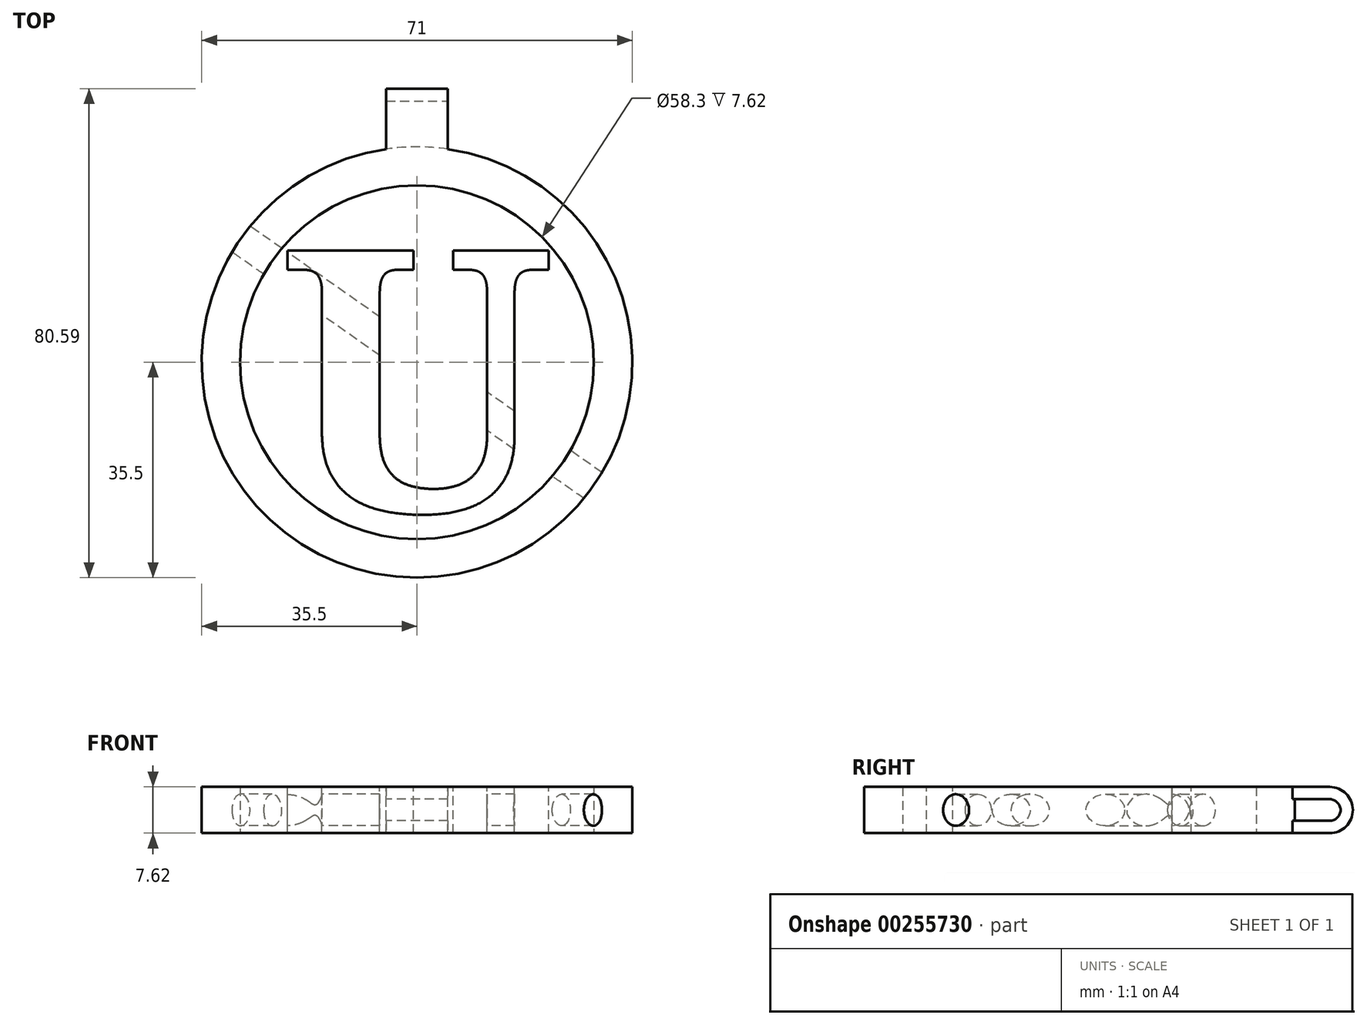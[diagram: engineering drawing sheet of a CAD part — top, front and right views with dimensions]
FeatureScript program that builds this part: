
annotation { "Feature Type Name" : "Feature", "Feature Type Description" : "" }
export const myFeature = defineFeature(function(context is Context, id is Id, definition is map)
    precondition{}
    {
        {
            var Q0;
            Q0=qCreatedBy(makeId("Top.planeOp"),FACE);
            var sketch = newSketch(context, id + "F0", { "sketchPlane" : qUnion([Q0])});
            skCircle(sketch, "E0", {"center": v(0, 0) * mm, "radius": 35.5 * mm});
            skCircle(sketch, "E1", {"center": v(0, 0) * mm, "radius": 29.15 * mm});
            skText(sketch, "E2", { "text": "U", "fontName": "NotoSerif-Bold.ttf"});
            const initialGuessF0  = {"E2": [-0.0225, -0.02528, 1, 0, 0.0438]};
            skSetInitialGuess(sketch, initialGuessF0);
            skSolve(sketch);
        }
        {
            var Q0;
            Q0 = qSketchRegion(id + "F0", true);
            extrude(context, id + "F1", {"entities" : qUnion([Q0]), "depth" : 7.62 * mm});
        }
        {
            var Q0;
            Q0=makeQuery(id+"F1.opExtrude","CAP_FACE",FACE,{"disambiguationData":[OSD([sQuery(id+"F0.wireOp",EDGE,"E0"),sQuery(id+"F0.wireOp",EDGE,"E1")])],"isStart":false});
            var sketch = newSketch(context, id + "F2", { "sketchPlane" : qUnion([Q0])});
            skText(sketch, "E3", { "text": "U", "fontName": "NotoSerif-Bold.ttf"});
            const initialGuessF2  = {"E3": [-0.02229, -0.02456, 1, 0, 0.04335]};
            skSetInitialGuess(sketch, initialGuessF2);
            skSolve(sketch);
        }
        {
            var Q0;
            Q0 = qSketchRegion(id + "F2", true);
            extrude(context, id + "F3", {"entities" : qUnion([Q0]), "oppositeDirection" : true, "depth" : 7.62 * mm});
        }
        {
            var Q0;
            Q0=qCreatedBy(makeId("Front.planeOp"),FACE);
            var Q1;
            Q1=makeQuery(id+"F3.opExtrude","SWEPT_EDGE",EDGE,{"disambiguationData":[OSD([sQuery(id+"F2.wireOp",EDGE,"E3.sketch_text.stroke-20"),sQuery(id+"F2.wireOp",EDGE,"E3.sketch_text.stroke-21")])]});
            cPlane(context, id + "F4", {"entities" : qUnion([Q0, Q1]), "cplaneType" : CPlaneType.LINE_ANGLE, "offset" : 25.4 * mm, "angle" : 55 * degree, "width" : 152.4 * mm, "height" : 152.4 * mm});
        }
        {
            var Q0;
            Q0=qCreatedBy(id+"F4.planeOp",FACE);
            var sketch = newSketch(context, id + "F5", { "sketchPlane" : qUnion([Q0])});
            skCircle(sketch, "E4", {"center": v(0, 3.81) * mm, "radius": 2.6 * mm});
            skSolve(sketch);
        }
        {
            var Q0;
            Q0 = qSketchRegion(id + "F5", true);
            extrude(context, id + "F6", {"entities" : qUnion([Q0]), "operationType" : NewBodyOperationType.REMOVE, "endBound" : BoundingType.THROUGH_ALL, "oppositeDirection" : true, "depth" : 25.4 * mm, "hasSecondDirection" : true, "secondDirectionBound" : SecondDirectionBoundingType.THROUGH_ALL, "secondDirectionOppositeDirection" : false, "secondDirectionDepth" : 25.4 * mm});
        }
        {
            var Q0;
            Q0=makeQuery(id+"F3.opExtrude","SWEPT_FACE",FACE,{"disambiguationData":[OSD([sQuery(id+"F2.wireOp",EDGE,"E3.sketch_text.stroke-44")])]});
            cPlane(context, id + "F7", {"entities" : qUnion([Q0]), "cplaneType" : CPlaneType.OFFSET, "offset" : 15.24 * mm, "width" : 152.4 * mm, "height" : 152.4 * mm});
        }
        {
            var Q0;
            Q0=qCreatedBy(id+"F7.planeOp",FACE);
            var sketch = newSketch(context, id + "F8", { "sketchPlane" : qUnion([Q0])});
            skLineSegment(sketch, "E5.bottom", {"start": v(-5.08, 7.62) * mm, "end": v(5.08, 7.62) * mm});
            skLineSegment(sketch, "E5.top", {"start": v(-5.08, 5.59) * mm, "end": v(5.08, 5.59) * mm});
            skLineSegment(sketch, "E5.left", {"start": v(-5.08, 7.62) * mm, "end": v(-5.08, 5.59) * mm});
            skLineSegment(sketch, "E5.right", {"start": v(5.08, 7.62) * mm, "end": v(5.08, 5.59) * mm});
            skLineSegment(sketch, "E6.bottom", {"start": v(-5.08, 2.03) * mm, "end": v(5.08, 2.03) * mm});
            skLineSegment(sketch, "E6.top", {"start": v(-5.08, 0) * mm, "end": v(5.08, 0) * mm});
            skLineSegment(sketch, "E6.left", {"start": v(-5.08, 2.03) * mm, "end": v(-5.08, 0) * mm});
            skLineSegment(sketch, "E6.right", {"start": v(5.08, 2.03) * mm, "end": v(5.08, 0) * mm});
            skSolve(sketch);
        }
        {
            var Q0;
            Q0 = qSketchRegion(id + "F8", true);
            extrude(context, id + "F9", {"entities" : qUnion([Q0]), "operationType" : NewBodyOperationType.ADD, "depth" : 7.62 * mm});
        }
        {
            var Q0;
            Q0=makeQuery(id+"F9.opExtrude","SWEPT_FACE",FACE,{"disambiguationData":[OSD([sQuery(id+"F8.wireOp",EDGE,"E5.left")])]});
            var sketch = newSketch(context, id + "F10", { "sketchPlane" : qUnion([Q0])});
            skArc(sketch, "E7", {"start": v(41.28, 0) * mm, "mid": v(45.1, 3.81) * mm, "end": v(41.28, 7.62) * mm});
            skArc(sketch, "E8", {"start": v(41.28, 2.03) * mm, "mid": v(43.06, 3.81) * mm, "end": v(41.28, 5.59) * mm});
            skLineSegment(sketch, "E9", {"start": v(41.28, 7.62) * mm, "end": v(41.28, 5.59) * mm});
            skLineSegment(sketch, "E10", {"start": v(41.28, 2.03) * mm, "end": v(41.28, 0) * mm});
            skSolve(sketch);
        }
        {
            var Q0;
            Q0 = qSketchRegion(id + "F10", true);
            extrude(context, id + "F11", {"entities" : qUnion([Q0]), "operationType" : NewBodyOperationType.ADD, "oppositeDirection" : true, "depth" : 10.16 * mm});
        }
    });
